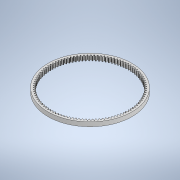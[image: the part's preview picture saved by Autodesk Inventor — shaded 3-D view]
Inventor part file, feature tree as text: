
AUTODESK INVENTOR PART (.ipt)
format: ipt  version: 2020 (Build 240168000, 168)  size: 1,055,232 bytes
history: native  units: mm
features: extrude x1, fillet x1, pattern_circular x1, sketch x1
ambient origin geometry x8: Origin, YZ Plane, XZ Plane, XY Plane, X Axis, Y Axis, Z Axis, Center Point
bodies: Solid1 (feature_tree)
feature tree (4):
  extrude  "Extrusion1"  Depth=0.4mm TaperAngle=360.0deg
  fillet  "Fillet2"  Radius=136.31068mm
  pattern_circular  "Circular Pattern2"  [2 undecoded]
  sketch  "Sketch1"  dims[d4=7.0mm d5=0.0mm d18=1030.0mm d19=360.0deg d23=136.31068mm d25=1.57767mm d26=1.262136mm d27=3.490659mm d28=122.160041mm d29=3.490659mm d30=0.315534mm d31=0.631068mm d32=0.991282mm d33=3.0mm d34=0.4mm d38=139.15534mm]
note: 2 required parameter values undecoded (feature->parameter linkage not recoverable at this tier; creation-order binding heuristic only, values carry confidence <= 0.55)
